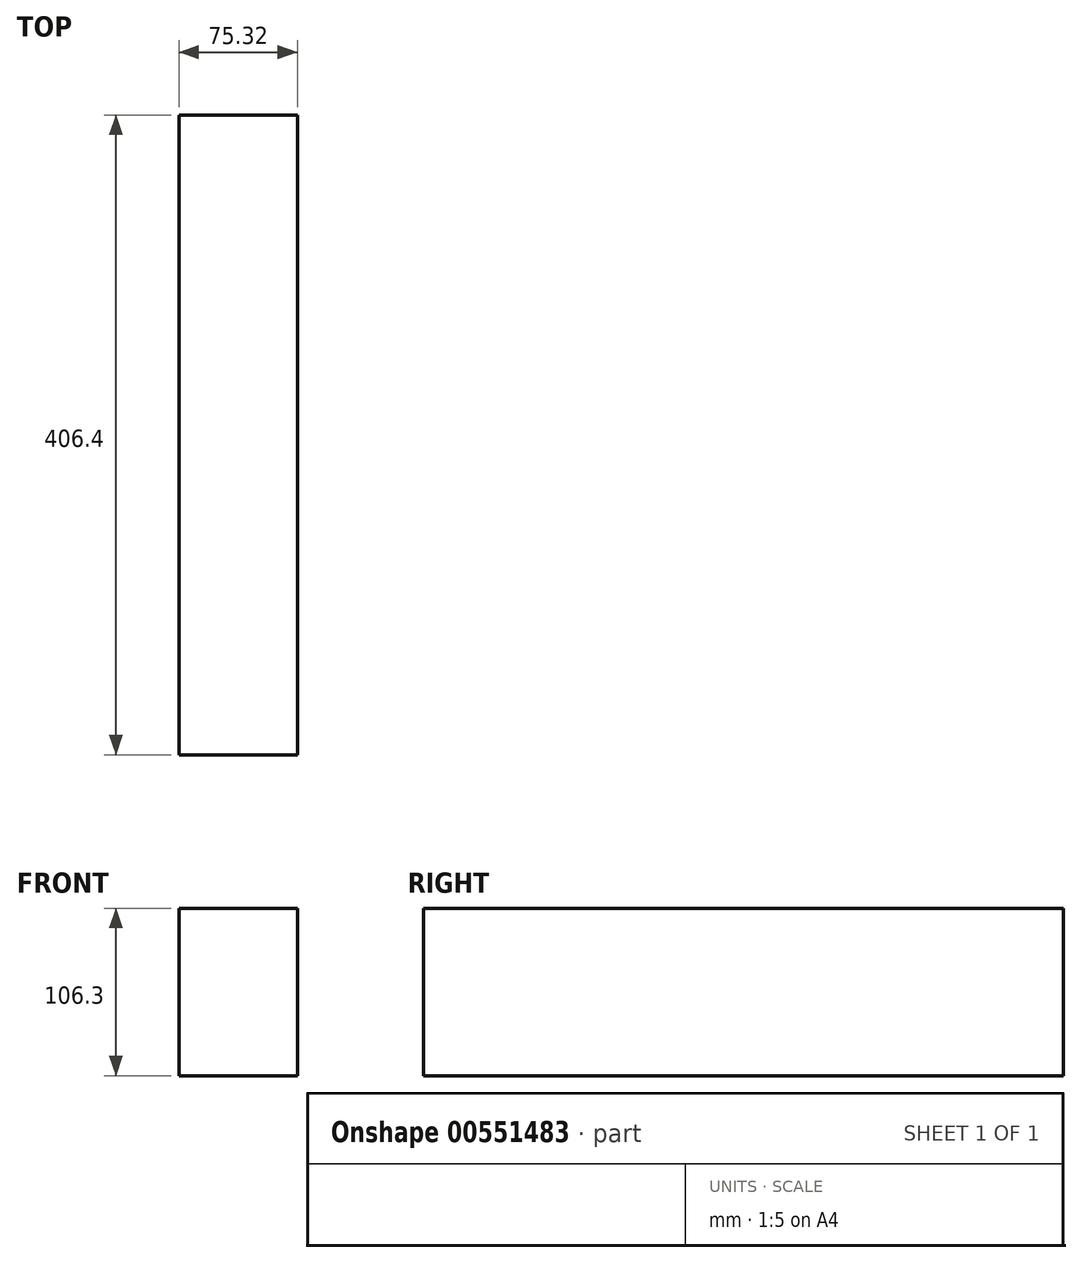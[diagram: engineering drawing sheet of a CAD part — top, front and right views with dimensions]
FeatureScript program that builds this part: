
annotation { "Feature Type Name" : "Feature", "Feature Type Description" : "" }
export const myFeature = defineFeature(function(context is Context, id is Id, definition is map)
    precondition{}
    {
        {
            var Q0;
            Q0=qCreatedBy(makeId("Front.planeOp"),FACE);
            var sketch = newSketch(context, id + "F0", { "sketchPlane" : qUnion([Q0])});
            skLineSegment(sketch, "E0.bottom", {"start": v(-37.66, 53.15) * mm, "end": v(37.66, 53.15) * mm});
            skLineSegment(sketch, "E0.top", {"start": v(-37.66, -53.15) * mm, "end": v(37.66, -53.15) * mm});
            skLineSegment(sketch, "E0.left", {"start": v(-37.66, 53.15) * mm, "end": v(-37.66, -53.15) * mm});
            skLineSegment(sketch, "E0.right", {"start": v(37.66, 53.15) * mm, "end": v(37.66, -53.15) * mm});
            skPoint(sketch, "E0.middle", {"position": v(0, 0) * mm});
            skSolve(sketch);
        }
        {
            var Q0;
            Q0 = qSketchRegion(id + "F0", true);
            extrude(context, id + "F1", {"entities" : qUnion([Q0]), "depth" : 406.4 * mm, "offsetDistance" : 25.4 * mm});
        }
    });
